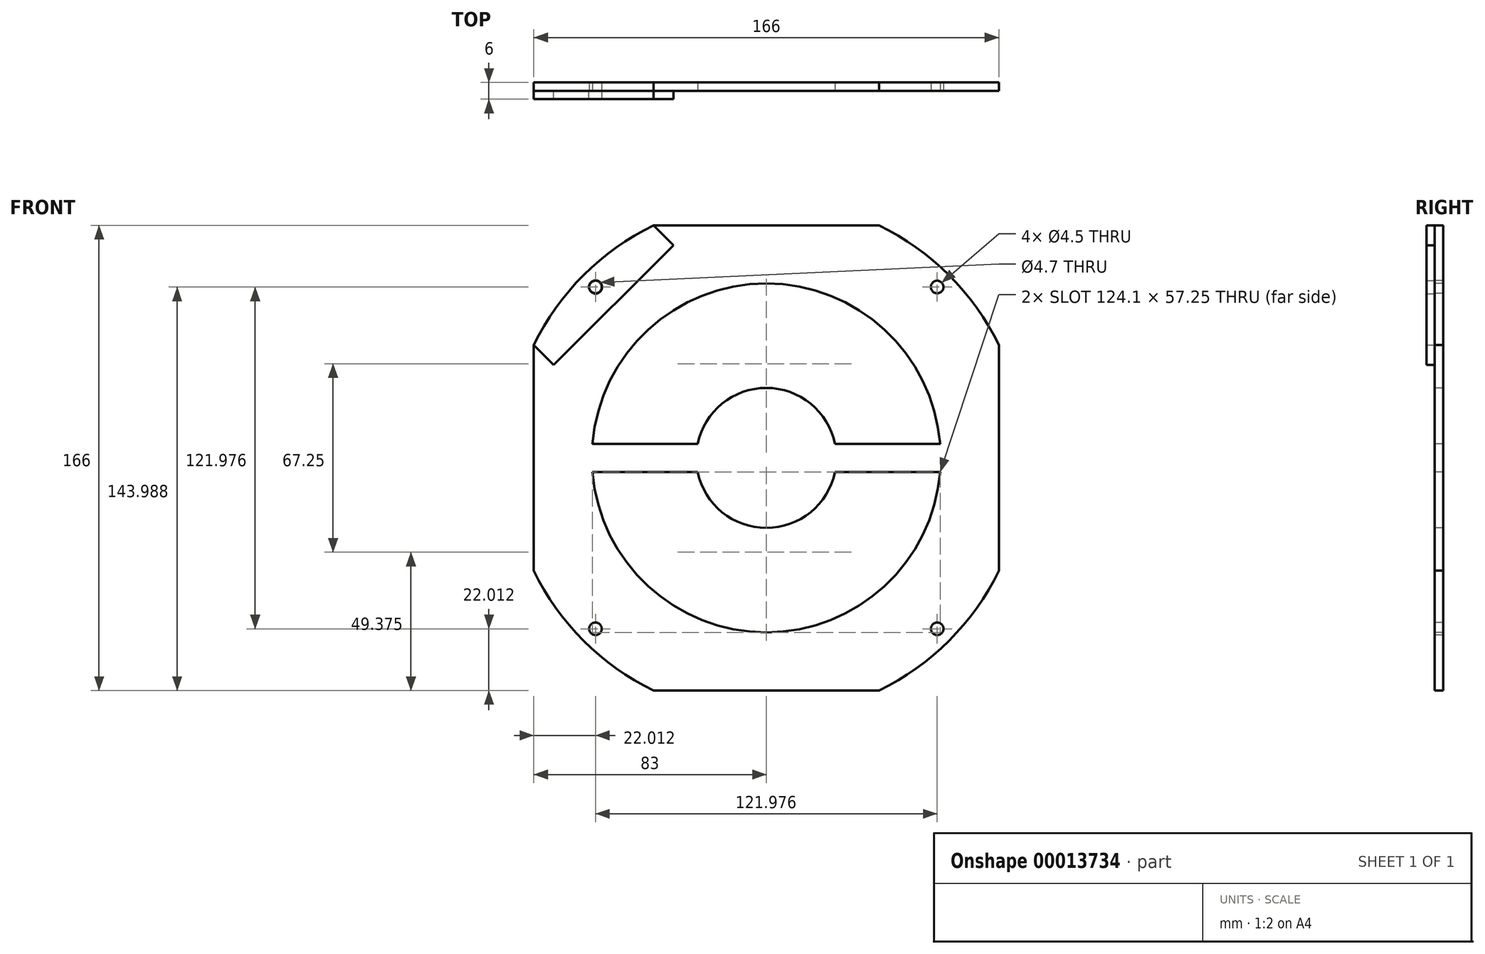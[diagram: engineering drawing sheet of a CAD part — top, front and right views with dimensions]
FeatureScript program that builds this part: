
annotation { "Feature Type Name" : "Feature", "Feature Type Description" : "" }
export const myFeature = defineFeature(function(context is Context, id is Id, definition is map)
    precondition{}
    {
        {
            var Q0;
            Q0=qCreatedBy(makeId("Front.planeOp"),FACE);
            var sketch = newSketch(context, id + "F0", { "sketchPlane" : qUnion([Q0])});
            skLineSegment(sketch, "E0.rect.bottom", {"start": v(83, -83) * mm, "end": v(-83, -83) * mm});
            skLineSegment(sketch, "E0.rect.top", {"start": v(83, 83) * mm, "end": v(-83, 83) * mm});
            skLineSegment(sketch, "E0.rect.left", {"start": v(83, -83) * mm, "end": v(83, 83) * mm});
            skLineSegment(sketch, "E0.rect.right", {"start": v(-83, -83) * mm, "end": v(-83, 83) * mm});
            skPoint(sketch, "E0.rect.middle", {"position": v(0, 0) * mm});
            skCircle(sketch, "E1", {"center": v(0, 0) * mm, "radius": 86.25 * mm, "construction": true});
            skArc(sketch, "E2", {"start": v(-40.26, 83) * mm, "mid": v(-65.23, 65.23) * mm, "end": v(-83, 40.26) * mm});
            skArc(sketch, "E3.1.0", {"start": v(-83, -40.26) * mm, "mid": v(-65.23, -65.23) * mm, "end": v(-40.26, -83) * mm});
            skArc(sketch, "E3.2.0", {"start": v(40.26, -83) * mm, "mid": v(65.23, -65.23) * mm, "end": v(83, -40.26) * mm});
            skArc(sketch, "E3.3.0", {"start": v(83, 40.26) * mm, "mid": v(65.23, 65.23) * mm, "end": v(40.26, 83) * mm});
            skSolve(sketch);
        }
        {
            var Q0;
            {var subQ3=sQuery(id+"F0.wireOp",EDGE,"E2");Q0=makeQuery(id+"F0.imprint","IMPRINT",FACE,{"disambiguationData":[TD([[makeQuery(id+"F0.imprint","IMPRINT",EDGE,{"derivedFrom":subQ3}),1.0]])]});}
            extrude(context, id + "F1", {"entities" : qUnion([Q0]), "depth" : 3 * mm});
        }
        {
            var Q0;
            Q0=makeQuery(id+"F1.opExtrude","CAP_FACE",FACE,{"disambiguationData":[OSD([sQuery(id+"F0.wireOp",EDGE,"E0.rect.bottom"),sQuery(id+"F0.wireOp",EDGE,"E0.rect.top"),sQuery(id+"F0.wireOp",EDGE,"E0.rect.left"),sQuery(id+"F0.wireOp",EDGE,"E0.rect.right"),sQuery(id+"F0.wireOp",EDGE,"E2"),sQuery(id+"F0.wireOp",EDGE,"E3.1.0"),sQuery(id+"F0.wireOp",EDGE,"E3.2.0"),sQuery(id+"F0.wireOp",EDGE,"E3.3.0")])],"isStart":false});
            var sketch = newSketch(context, id + "F2", { "sketchPlane" : qUnion([Q0])});
            skLineSegment(sketch, "E4", {"start": v(0, 0) * mm, "end": v(-60.99, 60.99) * mm, "construction": true});
            skLineSegment(sketch, "E5", {"start": v(0, 0) * mm, "end": v(-83, 0) * mm, "construction": true});
            skCircle(sketch, "E6", {"center": v(-60.99, 60.99) * mm, "radius": 2.25 * mm});
            skCircle(sketch, "E7.1.0", {"center": v(-60.99, -60.99) * mm, "radius": 2.25 * mm});
            skCircle(sketch, "E7.2.0", {"center": v(60.99, -60.99) * mm, "radius": 2.25 * mm});
            skCircle(sketch, "E7.3.0", {"center": v(60.99, 60.99) * mm, "radius": 2.25 * mm});
            skPoint(sketch, "E7.center", {"position": v(0, 0) * mm});
            skSolve(sketch);
        }
        {
            var Q0;
            Q0=makeQuery(id+"F2.imprint","IMPRINT",FACE,{"disambiguationData":[TD([[makeQuery(id+"F2.imprint","IMPRINT",EDGE,{"derivedFrom":sQuery(id+"F2.wireOp",EDGE,"E7.1.0")}),1.0]])]});
            var Q1;
            Q1=makeQuery(id+"F2.imprint","IMPRINT",FACE,{"disambiguationData":[TD([[makeQuery(id+"F2.imprint","IMPRINT",EDGE,{"derivedFrom":sQuery(id+"F2.wireOp",EDGE,"E7.2.0")}),1.0]])]});
            var Q2;
            Q2=makeQuery(id+"F2.imprint","IMPRINT",FACE,{"disambiguationData":[TD([[makeQuery(id+"F2.imprint","IMPRINT",EDGE,{"derivedFrom":sQuery(id+"F2.wireOp",EDGE,"E7.3.0")}),1.0]])]});
            var Q3;
            Q3=makeQuery(id+"F2.imprint","IMPRINT",FACE,{"disambiguationData":[TD([[makeQuery(id+"F2.imprint","IMPRINT",EDGE,{"derivedFrom":sQuery(id+"F2.wireOp",EDGE,"E6")}),1.0]])]});
            extrude(context, id + "F3", {"entities" : qUnion([Q0, Q1, Q2, Q3]), "operationType" : NewBodyOperationType.REMOVE, "endBound" : BoundingType.UP_TO_NEXT, "oppositeDirection" : true, "depth" : 25 * mm});
        }
        {
            var Q0;
            Q0=makeQuery(id+"F1.opExtrude","CAP_FACE",FACE,{"disambiguationData":[OSD([sQuery(id+"F0.wireOp",EDGE,"E0.rect.bottom"),sQuery(id+"F0.wireOp",EDGE,"E0.rect.top"),sQuery(id+"F0.wireOp",EDGE,"E0.rect.left"),sQuery(id+"F0.wireOp",EDGE,"E0.rect.right"),sQuery(id+"F0.wireOp",EDGE,"E2"),sQuery(id+"F0.wireOp",EDGE,"E3.1.0"),sQuery(id+"F0.wireOp",EDGE,"E3.2.0"),sQuery(id+"F0.wireOp",EDGE,"E3.3.0")])],"isStart":false});
            var sketch = newSketch(context, id + "F4", { "sketchPlane" : qUnion([Q0])});
            skCircle(sketch, "E8", {"center": v(0, 0) * mm, "radius": 62.25 * mm});
            skCircle(sketch, "E9", {"center": v(0, 0) * mm, "radius": 25 * mm});
            skLineSegment(sketch, "E10", {"start": v(-62.05, 5) * mm, "end": v(-24.5, 5) * mm});
            skLineSegment(sketch, "E11", {"start": v(-62.05, -5) * mm, "end": v(-24.5, -5) * mm});
            skLineSegment(sketch, "E12", {"start": v(24.5, 5) * mm, "end": v(62.05, 5) * mm});
            skLineSegment(sketch, "E13", {"start": v(24.5, -5) * mm, "end": v(62.05, -5) * mm});
            skSolve(sketch);
        }
        {
            var Q0;
            {var subQ1=sQuery(id+"F4.wireOp",EDGE,"E10");Q0=makeQuery(id+"F4.imprint","IMPRINT",FACE,{"disambiguationData":[TD([[makeQuery(id+"F4.imprint","IMPRINT",EDGE,{"derivedFrom":subQ1}),1.0]])]});}
            var Q1;
            {var subQ1=sQuery(id+"F4.wireOp",EDGE,"E11");Q1=makeQuery(id+"F4.imprint","IMPRINT",FACE,{"disambiguationData":[TD([[makeQuery(id+"F4.imprint","IMPRINT",EDGE,{"derivedFrom":subQ1}),-1.0]])]});}
            extrude(context, id + "F5", {"entities" : qUnion([Q0, Q1]), "operationType" : NewBodyOperationType.REMOVE, "endBound" : BoundingType.UP_TO_NEXT, "oppositeDirection" : true, "depth" : 25 * mm});
        }
        {
            var Q0;
            Q0=makeQuery(id+"F1.opExtrude","CAP_FACE",FACE,{"disambiguationData":[OSD([sQuery(id+"F0.wireOp",EDGE,"E0.rect.bottom"),sQuery(id+"F0.wireOp",EDGE,"E0.rect.top"),sQuery(id+"F0.wireOp",EDGE,"E0.rect.left"),sQuery(id+"F0.wireOp",EDGE,"E0.rect.right"),sQuery(id+"F0.wireOp",EDGE,"E2"),sQuery(id+"F0.wireOp",EDGE,"E3.1.0"),sQuery(id+"F0.wireOp",EDGE,"E3.2.0"),sQuery(id+"F0.wireOp",EDGE,"E3.3.0")])],"isStart":false});
            var sketch = newSketch(context, id + "F6", { "sketchPlane" : qUnion([Q0])});
            skArc(sketch, "E14.0", {"start": v(-40.26, 83) * mm, "mid": v(-65.23, 65.23) * mm, "end": v(-83, 40.26) * mm});
            skLineSegment(sketch, "E15", {"start": v(-83, 40.26) * mm, "end": v(-75.93, 33.2) * mm});
            skLineSegment(sketch, "E16", {"start": v(-75.93, 33.2) * mm, "end": v(-33.2, 75.93) * mm});
            skLineSegment(sketch, "E17", {"start": v(-33.2, 75.93) * mm, "end": v(-40.26, 83) * mm});
            skCircle(sketch, "E18.0", {"center": v(-60.99, 60.99) * mm, "radius": 2.35 * mm});
            skSolve(sketch);
        }
        {
            var Q0;
            Q0=makeQuery(id+"F6.imprint","IMPRINT",FACE,{"disambiguationData":[TD([[makeQuery(id+"F6.imprint","IMPRINT",EDGE,{"derivedFrom":sQuery(id+"F6.wireOp",EDGE,"E14.0")}),1.0]])]});
            extrude(context, id + "F7", {"entities" : qUnion([Q0]), "depth" : 3 * mm});
        }
    });
